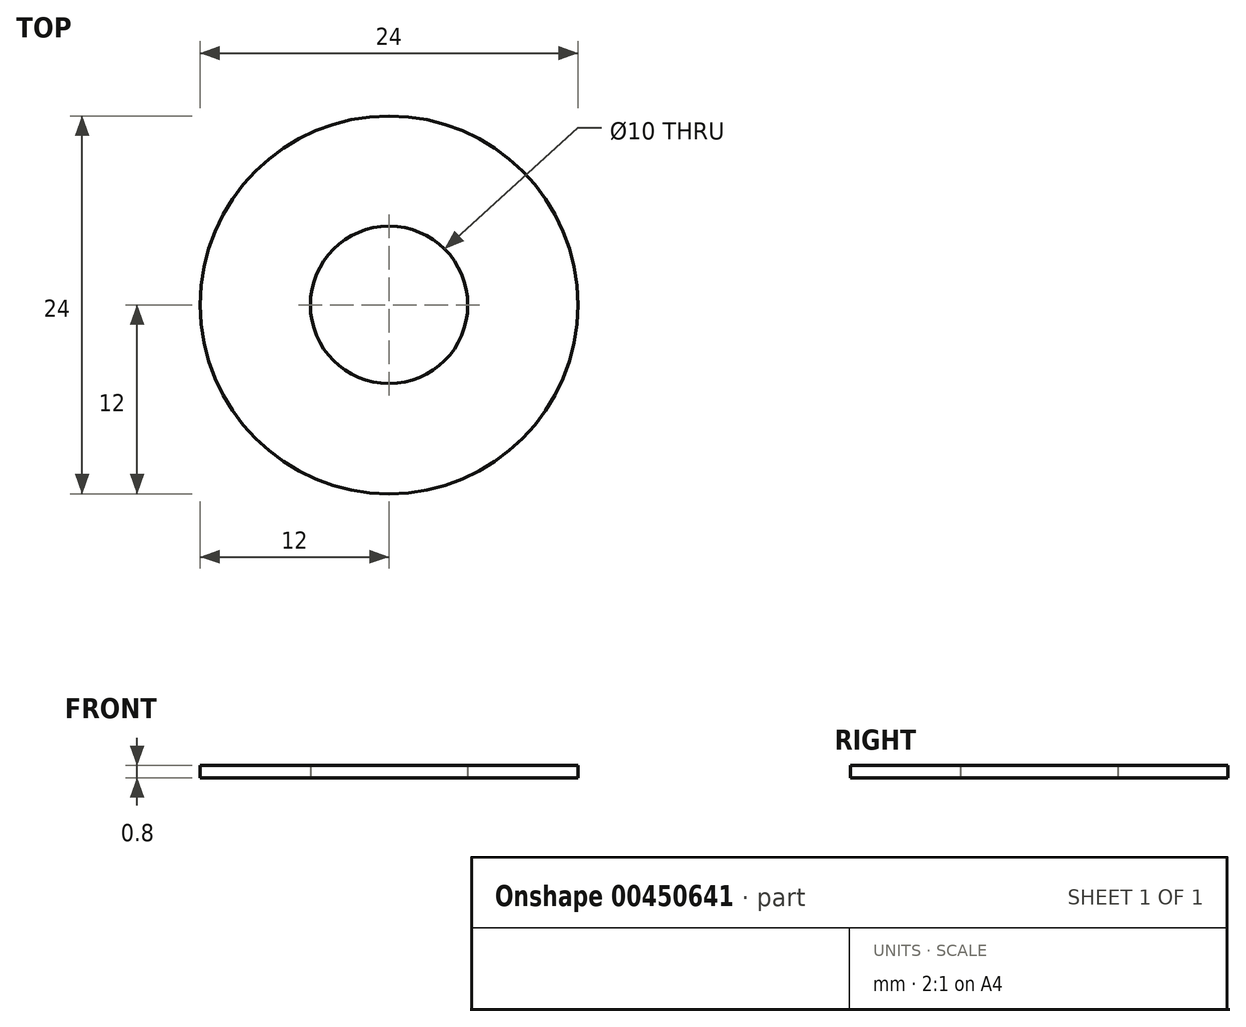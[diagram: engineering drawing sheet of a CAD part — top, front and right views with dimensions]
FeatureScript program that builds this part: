
annotation { "Feature Type Name" : "Feature", "Feature Type Description" : "" }
export const myFeature = defineFeature(function(context is Context, id is Id, definition is map)
    precondition{}
    {
        {
            var Q0;
            Q0=qCreatedBy(makeId("Top.planeOp"),FACE);
            var sketch = newSketch(context, id + "F0", { "sketchPlane" : qUnion([Q0])});
            skCircle(sketch, "E0", {"center": v(0, 0) * mm, "radius": 5 * mm});
            skCircle(sketch, "E1", {"center": v(0, 0) * mm, "radius": 12 * mm});
            skSolve(sketch);
        }
        {
            var Q0;
            Q0=makeQuery(id+"F0.imprint","IMPRINT",FACE,{"disambiguationData":[TD([[makeQuery(id+"F0.imprint","IMPRINT",EDGE,{"derivedFrom":sQuery(id+"F0.wireOp",EDGE,"E0")}),-1.0]])]});
            extrude(context, id + "F1", {"entities" : qUnion([Q0]), "depth" : .8 * mm});
        }
    });
